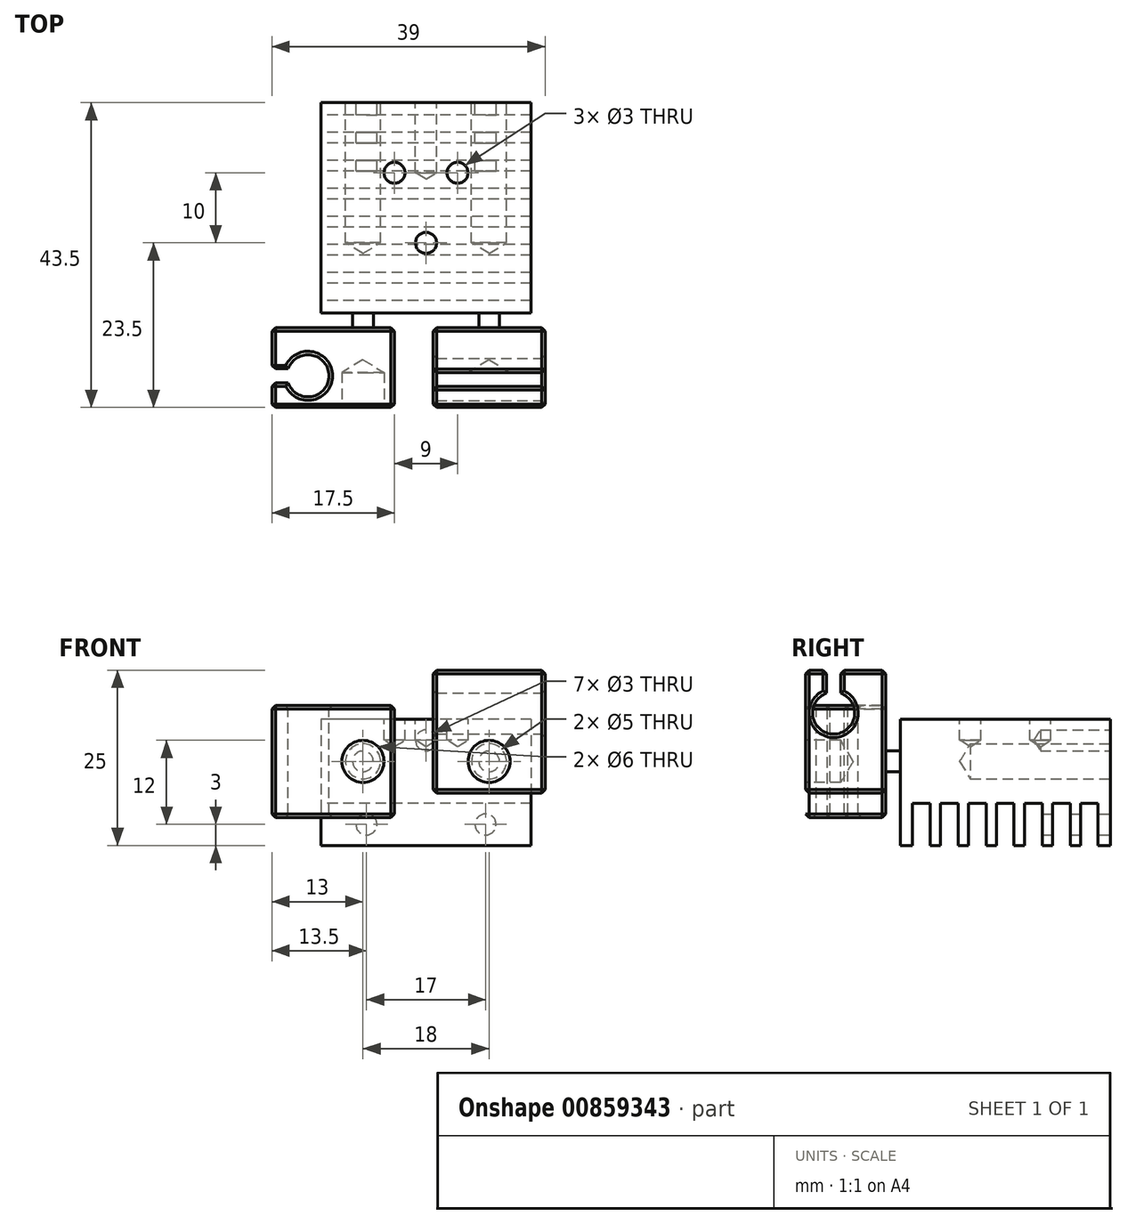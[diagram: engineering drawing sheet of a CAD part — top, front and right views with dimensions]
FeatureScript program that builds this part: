
annotation { "Feature Type Name" : "Feature", "Feature Type Description" : "" }
export const myFeature = defineFeature(function(context is Context, id is Id, definition is map)
    precondition{}
    {
        {
            var Q0;
            Q0=qCreatedBy(makeId("Top.planeOp"),FACE);
            var sketch = newSketch(context, id + "F0", { "sketchPlane" : qUnion([Q0])});
            skLineSegment(sketch, "E0.bottom", {"start": v(15, -15) * mm, "end": v(-15, -15) * mm});
            skLineSegment(sketch, "E0.top", {"start": v(15, 15) * mm, "end": v(-15, 15) * mm});
            skLineSegment(sketch, "E0.left", {"start": v(15, -15) * mm, "end": v(15, 15) * mm});
            skLineSegment(sketch, "E0.right", {"start": v(-15, -15) * mm, "end": v(-15, 15) * mm});
            skPoint(sketch, "E0.middle", {"position": v(0, 0) * mm});
            skSolve(sketch);
        }
        {
            var Q0;
            Q0=makeQuery(id+"F0.imprint","IMPRINT",FACE,{"disambiguationData":[TD([[makeQuery(id+"F0.imprint","IMPRINT",EDGE,{"derivedFrom":sQuery(id+"F0.wireOp",EDGE,"E0.bottom")}),-1.0]])]});
            extrude(context, id + "F11", {"entities" : qUnion([Q0]), "depth" : 18 * mm});
        }
        {
            var Q0;
            Q0=makeQuery(id+"F11.opExtrude","SWEPT_FACE",FACE,{"disambiguationData":[OSD([sQuery(id+"F0.wireOp",EDGE,"E0.top")])]});
            var sketch = newSketch(context, id + "F12", { "sketchPlane" : qUnion([Q0])});
            skPoint(sketch, "E1", {"position": v(-8.5, 3) * mm});
            skPoint(sketch, "E2", {"position": v(8.5, 3) * mm});
            skPoint(sketch, "E3", {"position": v(-9, 12) * mm});
            skPoint(sketch, "E4", {"position": v(9, 12) * mm});
            skPoint(sketch, "E5", {"position": v(0, 15) * mm});
            skPoint(sketch, "E6", {"position": v(-15, 18) * mm});
            skPoint(sketch, "E7", {"position": v(15, 18) * mm});
            skSolve(sketch);
        }
        {
            var Q0;
            Q0=sQuery(id+"F12.wireOp",VERTEX,"E3");
            var Q1;
            Q1=sQuery(id+"F12.wireOp",VERTEX,"E4");
            var Q2;
            Q2=makeQuery(id+"F11.opExtrude","SWEPT_BODY",BODY,{"disambiguationData":[OSD([sQuery(id+"F0.wireOp",EDGE,"E0.bottom"),sQuery(id+"F0.wireOp",EDGE,"E0.top"),sQuery(id+"F0.wireOp",EDGE,"E0.left"),sQuery(id+"F0.wireOp",EDGE,"E0.right")])]});
            hole(context, id + "F1", {"style" : HoleStyle.SIMPLE, "endStyle" : HoleEndStyle.BLIND, "holeDiameter" : 5 * mm, "holeDepth" : 20 * mm, "locations" : qUnion([Q0, Q1]), "scope" : qUnion([Q2])});
        }
        {
            var Q0;
            Q0=makeQuery(id+"F11.opExtrude","CAP_FACE",FACE,{"disambiguationData":[OSD([sQuery(id+"F0.wireOp",EDGE,"E0.bottom"),sQuery(id+"F0.wireOp",EDGE,"E0.top"),sQuery(id+"F0.wireOp",EDGE,"E0.left"),sQuery(id+"F0.wireOp",EDGE,"E0.right")])],"isStart":true});
            var sketch = newSketch(context, id + "F13", { "sketchPlane" : qUnion([Q0])});
            skLineSegment(sketch, "E8.bottom", {"start": v(15, -13.25) * mm, "end": v(-15.01, -13.25) * mm});
            skLineSegment(sketch, "E8.top", {"start": v(15, -10.75) * mm, "end": v(-15.01, -10.75) * mm});
            skLineSegment(sketch, "E8.left", {"start": v(15, -13.25) * mm, "end": v(15, -10.75) * mm});
            skLineSegment(sketch, "E8.right", {"start": v(-15.01, -13.25) * mm, "end": v(-15.01, -10.75) * mm});
            skLineSegment(sketch, "E9.0.1.0", {"start": v(15, -9.25) * mm, "end": v(15, -6.75) * mm});
            skLineSegment(sketch, "E9.0.1.1", {"start": v(-15.01, -9.25) * mm, "end": v(-15.01, -6.75) * mm});
            skLineSegment(sketch, "E9.0.1.2", {"start": v(15, -9.25) * mm, "end": v(-15.01, -9.25) * mm});
            skLineSegment(sketch, "E9.0.1.3", {"start": v(15, -6.75) * mm, "end": v(-15.01, -6.75) * mm});
            skLineSegment(sketch, "E9.0.2.0", {"start": v(15, -5.25) * mm, "end": v(15, -2.75) * mm});
            skLineSegment(sketch, "E9.0.2.1", {"start": v(-15.01, -5.25) * mm, "end": v(-15.01, -2.75) * mm});
            skLineSegment(sketch, "E9.0.2.2", {"start": v(15, -5.25) * mm, "end": v(-15.01, -5.25) * mm});
            skLineSegment(sketch, "E9.0.2.3", {"start": v(15, -2.75) * mm, "end": v(-15.01, -2.75) * mm});
            skLineSegment(sketch, "E9.0.3.0", {"start": v(15, -1.25) * mm, "end": v(15, 1.25) * mm});
            skLineSegment(sketch, "E9.0.3.1", {"start": v(-15.01, -1.25) * mm, "end": v(-15.01, 1.25) * mm});
            skLineSegment(sketch, "E9.0.3.2", {"start": v(15, -1.25) * mm, "end": v(-15.01, -1.25) * mm});
            skLineSegment(sketch, "E9.0.3.3", {"start": v(15, 1.25) * mm, "end": v(-15.01, 1.25) * mm});
            skLineSegment(sketch, "E9.0.4.0", {"start": v(15, 2.75) * mm, "end": v(15, 5.25) * mm});
            skLineSegment(sketch, "E9.0.4.1", {"start": v(-15.01, 2.75) * mm, "end": v(-15.01, 5.25) * mm});
            skLineSegment(sketch, "E9.0.4.2", {"start": v(15, 2.75) * mm, "end": v(-15.01, 2.75) * mm});
            skLineSegment(sketch, "E9.0.4.3", {"start": v(15, 5.25) * mm, "end": v(-15.01, 5.25) * mm});
            skLineSegment(sketch, "E9.0.5.0", {"start": v(15, 6.75) * mm, "end": v(15, 9.25) * mm});
            skLineSegment(sketch, "E9.0.5.1", {"start": v(-15.01, 6.75) * mm, "end": v(-15.01, 9.25) * mm});
            skLineSegment(sketch, "E9.0.5.2", {"start": v(15, 6.75) * mm, "end": v(-15.01, 6.75) * mm});
            skLineSegment(sketch, "E9.0.5.3", {"start": v(15, 9.25) * mm, "end": v(-15.01, 9.25) * mm});
            skLineSegment(sketch, "E9.0.6.0", {"start": v(15, 10.75) * mm, "end": v(15, 13.25) * mm});
            skLineSegment(sketch, "E9.0.6.1", {"start": v(-15.01, 10.75) * mm, "end": v(-15.01, 13.25) * mm});
            skLineSegment(sketch, "E9.0.6.2", {"start": v(15, 10.75) * mm, "end": v(-15.01, 10.75) * mm});
            skLineSegment(sketch, "E9.0.6.3", {"start": v(15, 13.25) * mm, "end": v(-15.01, 13.25) * mm});
            skLineSegment(sketch, "E9.direction1", {"start": v(-15.01, -13.25) * mm, "end": v(9.99, -13.25) * mm, "construction": true});
            skLineSegment(sketch, "E9.direction2", {"start": v(-15.01, -13.25) * mm, "end": v(-15.01, -9.25) * mm, "construction": true});
            skSolve(sketch);
        }
        {
            var Q0;
            {var subQ0=sQuery(id+"F13.wireOp",EDGE,"E9.0.6.0");Q0=makeQuery(id+"F13.imprint","IMPRINT",FACE,{"disambiguationData":[TD([[makeQuery(id+"F13.imprint","IMPRINT",EDGE,{"derivedFrom":subQ0}),-1.0]])]});}
            var Q1;
            {var subQ0=sQuery(id+"F13.wireOp",EDGE,"E9.0.5.0");Q1=makeQuery(id+"F13.imprint","IMPRINT",FACE,{"disambiguationData":[TD([[makeQuery(id+"F13.imprint","IMPRINT",EDGE,{"derivedFrom":subQ0}),-1.0]])]});}
            var Q2;
            {var subQ0=sQuery(id+"F13.wireOp",EDGE,"E9.0.4.0");Q2=makeQuery(id+"F13.imprint","IMPRINT",FACE,{"disambiguationData":[TD([[makeQuery(id+"F13.imprint","IMPRINT",EDGE,{"derivedFrom":subQ0}),-1.0]])]});}
            var Q3;
            {var subQ0=sQuery(id+"F13.wireOp",EDGE,"E9.0.3.0");Q3=makeQuery(id+"F13.imprint","IMPRINT",FACE,{"disambiguationData":[TD([[makeQuery(id+"F13.imprint","IMPRINT",EDGE,{"derivedFrom":subQ0}),-1.0]])]});}
            var Q4;
            {var subQ0=sQuery(id+"F13.wireOp",EDGE,"E9.0.2.0");Q4=makeQuery(id+"F13.imprint","IMPRINT",FACE,{"disambiguationData":[TD([[makeQuery(id+"F13.imprint","IMPRINT",EDGE,{"derivedFrom":subQ0}),-1.0]])]});}
            var Q5;
            {var subQ0=sQuery(id+"F13.wireOp",EDGE,"E9.0.1.0");Q5=makeQuery(id+"F13.imprint","IMPRINT",FACE,{"disambiguationData":[TD([[makeQuery(id+"F13.imprint","IMPRINT",EDGE,{"derivedFrom":subQ0}),-1.0]])]});}
            var Q6;
            {var subQ0=sQuery(id+"F13.wireOp",EDGE,"E8.left");Q6=makeQuery(id+"F13.imprint","IMPRINT",FACE,{"disambiguationData":[TD([[makeQuery(id+"F13.imprint","IMPRINT",EDGE,{"derivedFrom":subQ0}),-1.0]])]});}
            extrude(context, id + "F14", {"entities" : qUnion([Q0, Q1, Q2, Q3, Q4, Q5, Q6]), "operationType" : NewBodyOperationType.REMOVE, "oppositeDirection" : true, "depth" : 6 * mm});
        }
        {
            var Q0;
            Q0=makeQuery(id+"F11.opExtrude","CAP_FACE",FACE,{"disambiguationData":[OSD([sQuery(id+"F0.wireOp",EDGE,"E0.bottom"),sQuery(id+"F0.wireOp",EDGE,"E0.top"),sQuery(id+"F0.wireOp",EDGE,"E0.left"),sQuery(id+"F0.wireOp",EDGE,"E0.right")])],"isStart":false});
            var sketch = newSketch(context, id + "F2", { "sketchPlane" : qUnion([Q0])});
            skPoint(sketch, "E10", {"position": v(-4.5, 5) * mm});
            skPoint(sketch, "E11", {"position": v(4.5, 5) * mm});
            skPoint(sketch, "E12", {"position": v(0, -5) * mm});
            skSolve(sketch);
        }
        {
            var Q0;
            Q0=sQuery(id+"F2.wireOp",VERTEX,"E11");
            var Q1;
            Q1=sQuery(id+"F2.wireOp",VERTEX,"E10");
            var Q2;
            Q2=sQuery(id+"F2.wireOp",VERTEX,"E12");
            var Q3;
            Q3=makeQuery(id+"F11.opExtrude","SWEPT_BODY",BODY,{"disambiguationData":[OSD([sQuery(id+"F0.wireOp",EDGE,"E0.bottom"),sQuery(id+"F0.wireOp",EDGE,"E0.top"),sQuery(id+"F0.wireOp",EDGE,"E0.left"),sQuery(id+"F0.wireOp",EDGE,"E0.right")])]});
            hole(context, id + "F15", {"style" : HoleStyle.SIMPLE, "endStyle" : HoleEndStyle.BLIND, "holeDiameter" : 3 * mm, "holeDepth" : 3 * mm, "locations" : qUnion([Q0, Q1, Q2]), "scope" : qUnion([Q3])});
        }
        {
            var Q0;
            Q0=sQuery(id+"F12.wireOp",VERTEX,"E2");
            var Q1;
            Q1=sQuery(id+"F12.wireOp",VERTEX,"E1");
            var Q2;
            Q2=sQuery(id+"F12.wireOp",VERTEX,"E5");
            var Q3;
            Q3=makeQuery(id+"F11.opExtrude","SWEPT_BODY",BODY,{"disambiguationData":[OSD([sQuery(id+"F0.wireOp",EDGE,"E0.bottom"),sQuery(id+"F0.wireOp",EDGE,"E0.top"),sQuery(id+"F0.wireOp",EDGE,"E0.left"),sQuery(id+"F0.wireOp",EDGE,"E0.right")])]});
            hole(context, id + "F16", {"style" : HoleStyle.SIMPLE, "endStyle" : HoleEndStyle.BLIND, "holeDiameter" : 3 * mm, "holeDepth" : 10 * mm, "locations" : qUnion([Q0, Q1, Q2]), "scope" : qUnion([Q3])});
        }
        {
            var Q0;
            Q0=makeQuery(id+"F11.opExtrude","SWEPT_FACE",FACE,{"disambiguationData":[OSD([sQuery(id+"F0.wireOp",EDGE,"E0.bottom")])]});
            var sketch = newSketch(context, id + "F3", { "sketchPlane" : qUnion([Q0])});
            skCircle(sketch, "E13", {"center": v(9, 12) * mm, "radius": 1.48 * mm});
            skCircle(sketch, "E14", {"center": v(-9, 12) * mm, "radius": 1.48 * mm});
            skSolve(sketch);
        }
        {
            var Q0;
            Q0=makeQuery(id+"F3.imprint","IMPRINT",FACE,{"disambiguationData":[TD([[makeQuery(id+"F3.imprint","IMPRINT",EDGE,{"derivedFrom":sQuery(id+"F3.wireOp",EDGE,"E14")}),1.0]])]});
            var Q1;
            Q1=makeQuery(id+"F3.imprint","IMPRINT",FACE,{"disambiguationData":[TD([[makeQuery(id+"F3.imprint","IMPRINT",EDGE,{"derivedFrom":sQuery(id+"F3.wireOp",EDGE,"E13")}),1.0]])]});
            extrude(context, id + "F4", {"entities" : qUnion([Q0, Q1]), "operationType" : NewBodyOperationType.ADD, "depth" : 2.1 * mm});
        }
        {
            var Q0;
            Q0=makeQuery(id+"F4.opExtrude","CAP_FACE",FACE,{"disambiguationData":[OSD([sQuery(id+"F3.wireOp",EDGE,"E13")])],"isStart":false});
            var sketch = newSketch(context, id + "F17", { "sketchPlane" : qUnion([Q0])});
            skLineSegment(sketch, "E15.bottom", {"start": v(1, 25) * mm, "end": v(17, 25) * mm});
            skLineSegment(sketch, "E15.top", {"start": v(1, 7.5) * mm, "end": v(17, 7.5) * mm});
            skLineSegment(sketch, "E15.left", {"start": v(1, 25) * mm, "end": v(1, 7.5) * mm});
            skLineSegment(sketch, "E15.right", {"start": v(17, 25) * mm, "end": v(17, 7.5) * mm});
            skPoint(sketch, "E16", {"position": v(9, 12) * mm});
            skSolve(sketch);
        }
        {
            var Q0;
            Q0=makeQuery(id+"F4.opExtrude","CAP_FACE",FACE,{"disambiguationData":[OSD([sQuery(id+"F3.wireOp",EDGE,"E14")])],"isStart":false});
            var sketch = newSketch(context, id + "F18", { "sketchPlane" : qUnion([Q0])});
            skPoint(sketch, "E17", {"position": v(-9, 12) * mm});
            skLineSegment(sketch, "E18.bottom", {"start": v(-22, 20) * mm, "end": v(-4.5, 20) * mm});
            skLineSegment(sketch, "E18.top", {"start": v(-22, 4) * mm, "end": v(-4.5, 4) * mm});
            skLineSegment(sketch, "E18.left", {"start": v(-22, 20) * mm, "end": v(-22, 4) * mm});
            skLineSegment(sketch, "E18.right", {"start": v(-4.5, 20) * mm, "end": v(-4.5, 4) * mm});
            skSolve(sketch);
        }
        {
            var Q0;
            Q0=qSketchRegion(id+"F18",true);
            var Q1;
            Q1=qSketchRegion(id+"F17",true);
            extrude(context, id + "F19", {"entities" : qUnion([Q0, Q1]), "operationType" : NewBodyOperationType.ADD, "depth" : 11.4 * mm});
        }
        {
            var Q0;
            Q0=makeQuery(id+"F19.opExtrude","CAP_FACE",FACE,{"disambiguationData":[OSD([sQuery(id+"F17.wireOp",EDGE,"E15.bottom"),sQuery(id+"F17.wireOp",EDGE,"E15.top"),sQuery(id+"F17.wireOp",EDGE,"E15.left"),sQuery(id+"F17.wireOp",EDGE,"E15.right")])],"isStart":false});
            var sketch = newSketch(context, id + "F20", { "sketchPlane" : qUnion([Q0])});
            skPoint(sketch, "E19", {"position": v(9, 12) * mm});
            skPoint(sketch, "E19.positionSnap0", {"position": v(9, 7.5) * mm});
            skSolve(sketch);
        }
        {
            var Q0;
            Q0=makeQuery(id+"F19.opExtrude","CAP_FACE",FACE,{"disambiguationData":[OSD([sQuery(id+"F18.wireOp",EDGE,"E18.bottom"),sQuery(id+"F18.wireOp",EDGE,"E18.top"),sQuery(id+"F18.wireOp",EDGE,"E18.left"),sQuery(id+"F18.wireOp",EDGE,"E18.right")])],"isStart":false});
            var sketch = newSketch(context, id + "F21", { "sketchPlane" : qUnion([Q0])});
            skPoint(sketch, "E20", {"position": v(-9, 12) * mm});
            skPoint(sketch, "E20.positionSnap0", {"position": v(-13.25, 20) * mm});
            skSolve(sketch);
        }
        {
            var Q0;
            Q0=sQuery(id+"F21.wireOp",VERTEX,"E20");
            var Q1;
            Q1=sQuery(id+"F20.wireOp",VERTEX,"E19");
            var Q2;
            Q2=makeQuery(id+"F11.opExtrude","SWEPT_BODY",BODY,{"disambiguationData":[OSD([sQuery(id+"F0.wireOp",EDGE,"E0.bottom"),sQuery(id+"F0.wireOp",EDGE,"E0.top"),sQuery(id+"F0.wireOp",EDGE,"E0.left"),sQuery(id+"F0.wireOp",EDGE,"E0.right")])]});
            hole(context, id + "F5", {"style" : HoleStyle.SIMPLE, "endStyle" : HoleEndStyle.BLIND, "holeDiameter" : 6 * mm, "holeDepth" : 5 * mm, "locations" : qUnion([Q0, Q1]), "scope" : qUnion([Q2])});
        }
        {
            var Q0;
            Q0=makeQuery(id+"F19.opExtrude","SWEPT_FACE",FACE,{"disambiguationData":[OSD([sQuery(id+"F17.wireOp",EDGE,"E15.right")])]});
            var sketch = newSketch(context, id + "F6", { "sketchPlane" : qUnion([Q0])});
            skArc(sketch, "E21", {"start": v(-25.5, 21.73) * mm, "mid": v(-24.5, 15.9) * mm, "end": v(-23.5, 21.73) * mm});
            skLineSegment(sketch, "E22.bottom", {"start": v(-25.5, 30.74) * mm, "end": v(-23.5, 30.74) * mm});
            skLineSegment(sketch, "E22.top", {"start": v(-25.5, 7.06) * mm, "end": v(-23.5, 7.06) * mm});
            skLineSegment(sketch, "E22.left", {"start": v(-25.5, 30.74) * mm, "end": v(-25.5, 21.73) * mm});
            skLineSegment(sketch, "E22.right", {"start": v(-23.5, 30.74) * mm, "end": v(-23.5, 21.73) * mm});
            skSolve(sketch);
        }
        {
            var Q0;
            Q0=makeQuery(id+"F19.opExtrude","SWEPT_FACE",FACE,{"disambiguationData":[OSD([sQuery(id+"F18.wireOp",EDGE,"E18.bottom")])]});
            var sketch = newSketch(context, id + "F7", { "sketchPlane" : qUnion([Q0])});
            skArc(sketch, "E23", {"start": v(-19.67, -24.98) * mm, "mid": v(-13.84, -23.98) * mm, "end": v(-19.67, -22.98) * mm});
            skLineSegment(sketch, "E24.top", {"start": v(-23.34, -24.98) * mm, "end": v(-23.34, -22.98) * mm});
            skLineSegment(sketch, "E24.left", {"start": v(-10.34, -24.98) * mm, "end": v(-14.02, -24.98) * mm});
            skLineSegment(sketch, "E24.right", {"start": v(-19.67, -22.98) * mm, "end": v(-23.34, -22.98) * mm});
            skPoint(sketch, "E25.orphan", {"position": v(-10.34, -22.98) * mm});
            skLineSegment(sketch, "E26.trimOffspring", {"start": v(-19.67, -24.98) * mm, "end": v(-23.34, -24.98) * mm});
            skSolve(sketch);
        }
        {
            var Q0;
            {var subQ0=sQuery(id+"F6.wireOp",EDGE,"E21");Q0=makeQuery(id+"F6.imprint","IMPRINT",FACE,{"disambiguationData":[TD([[makeQuery(id+"F6.imprint","IMPRINT",EDGE,{"derivedFrom":subQ0}),1.0]])]});}
            extrude(context, id + "F8", {"entities" : qUnion([Q0]), "operationType" : NewBodyOperationType.REMOVE, "endBound" : BoundingType.UP_TO_NEXT, "oppositeDirection" : true, "depth" : 25 * mm});
        }
        {
            var Q0;
            {var subQ1=sQuery(id+"F7.wireOp",EDGE,"E23");var subQ9=makeQuery(id+"F7.imprint","IMPRINT",VERTEX,{"derivedFrom":subQ1});Q0=makeQuery(id+"F7.imprint","IMPRINT",FACE,{"disambiguationData":[TD([[makeQuery(id+"F7.imprint","IMPRINT",EDGE,{"disambiguationData":[TD([[subQ9,1.0]])],"derivedFrom":subQ1}),1.0]])]});}
            var Q1;
            {var subQ0=sQuery(id+"F7.wireOp",EDGE,"E24.top");Q1=makeQuery(id+"F7.imprint","IMPRINT",FACE,{"disambiguationData":[TD([[makeQuery(id+"F7.imprint","IMPRINT",EDGE,{"derivedFrom":subQ0}),-1.0]])]});}
            extrude(context, id + "F22", {"entities" : qUnion([Q0, Q1]), "operationType" : NewBodyOperationType.REMOVE, "endBound" : BoundingType.UP_TO_NEXT, "oppositeDirection" : true, "depth" : 25 * mm});
        }
        {
            var Q0;
            Q0=makeQuery(id+"F19.opExtrude","SWEPT_FACE",FACE,{"disambiguationData":[OSD([sQuery(id+"F17.wireOp",EDGE,"E15.right")])]});
            var Q1;
            Q1=makeQuery(id+"F19.opExtrude","SWEPT_FACE",FACE,{"disambiguationData":[OSD([sQuery(id+"F17.wireOp",EDGE,"E15.top")])]});
            var Q2;
            Q2=makeQuery(id+"F19.opExtrude","SWEPT_FACE",FACE,{"disambiguationData":[OSD([sQuery(id+"F18.wireOp",EDGE,"E18.top")])]});
            var Q3;
            Q3=makeQuery(id+"F19.opExtrude","SWEPT_FACE",FACE,{"disambiguationData":[OSD([sQuery(id+"F18.wireOp",EDGE,"E18.right")])]});
            var Q4;
            {var subQ2=sQuery(id+"F17.wireOp",EDGE,"E15.bottom");Q4=makeQuery(id+"F8.boolean.opBoolean","SPLIT",FACE,{"disambiguationData":[TD([makeQuery(id+"F8.opExtrude","SWEPT_FACE",FACE,{"disambiguationData":[OSD([sQuery(id+"F6.wireOp",EDGE,"E22.right")])]})])],"derivedFrom":makeQuery(id+"F19.opExtrude","SWEPT_FACE",FACE,{"disambiguationData":[OSD([subQ2])]})});}
            var Q5;
            {var subQ2=sQuery(id+"F17.wireOp",EDGE,"E15.bottom");Q5=makeQuery(id+"F8.boolean.opBoolean","SPLIT",FACE,{"disambiguationData":[TD([makeQuery(id+"F8.opExtrude","SWEPT_FACE",FACE,{"disambiguationData":[OSD([sQuery(id+"F6.wireOp",EDGE,"E22.left")])]})])],"derivedFrom":makeQuery(id+"F19.opExtrude","SWEPT_FACE",FACE,{"disambiguationData":[OSD([subQ2])]})});}
            var Q6;
            Q6=makeQuery(id+"F19.opExtrude","SWEPT_FACE",FACE,{"disambiguationData":[OSD([sQuery(id+"F18.wireOp",EDGE,"E18.bottom")])]});
            var Q7;
            Q7=makeQuery(id+"F19.opExtrude","SWEPT_FACE",FACE,{"disambiguationData":[OSD([sQuery(id+"F18.wireOp",EDGE,"E18.left")])]});
            var Q8;
            Q8=makeQuery(id+"F19.opExtrude","SWEPT_FACE",FACE,{"disambiguationData":[OSD([sQuery(id+"F17.wireOp",EDGE,"E15.left")])]});
            chamfer(context, id + "F9", {"entities" : qUnion([Q0, Q1, Q2, Q3, Q4, Q5, Q6, Q7, Q8]), "width" : 0.5 * mm, "tangentPropagation" : true});
        }
    });
